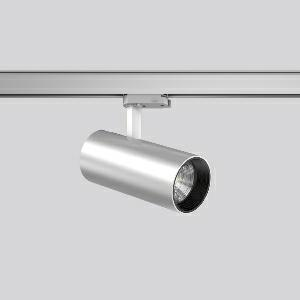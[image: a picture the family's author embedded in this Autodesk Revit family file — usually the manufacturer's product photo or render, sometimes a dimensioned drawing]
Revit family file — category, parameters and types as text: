
# Revit family: deecos_s_mini_742206_004_2_962b
name_source: partatom
category: Lighting Fixtures
units: mm (PartAtom-declared; Revit-internal decimal feet)

## family parameters
Cut with Voids When Loaded = No
Host = Face
Light Source = No
Part Type = Normal
Room Calculation Point = No
Round Connector Dimension = Use Diameter
Shared = No

## types (1)
- DEECOS S mini (1 x LED Modul 927, 3000 lm, 2700)
    Apparent Load = 29 VA
    Approval mark = CE
    CIE Flux Codes = 99 100 100 100 100
    Color Rendering = 92
    Color Temperature = 2700
    Default Elevation = 1800 mm
    Description = Series: DEECOS S mini
LED surface-mounted projector in modern design with no visible cooling ribs. Housing: die-cast aluminium, powder-coated. Rotation range: 356°. Swivel range: 90°. Black plastic ring and recessed LED to prevent glare from the side. Optical assembly with lens made of plastic (polycarbonate) for the best homogeneous light distribution - can be changed without tools. Best colour rendering index Ra>90. With multi adaptor for 3-circuit tracks 230 V. Suitable for Track on ceiling, Wall track. High quality converter without flickering and stroboscopic effect. The following accessories can be mounted without use of tools: interchangeable lenses, decorative glasses, honeycomb louvre, clear and frosted diffusers, white interchangeable plastic ring. 
Colour: silver
Diameter: 87 mm
Height: 214 mm
Lamp: LED
Socket: without socket
Colour temperature: 2700K
Colour rendering index (CRI): 92
System power: 29 W
Rated luminous flux: 3000 lm
Luminous efficiency: 103 lm/W
Control gear: Regulated power supply
Protection class: I
Type of protection: IP 20
    Height = 214 mm
    Lamp = 1 x LED Modul 927
    Lamp Light Flux = 3000 lm
    Lamp count = 1
    Length = 87 mm
    Lifetime = 50000 h
    Luminous efficacy = 103 lm/W
    Manufacturer = RZB
    ModVariant = No
    Model = 742206.004.2
    Mounting Place = Ceiling
    Mounting Type = Rail mounted
    Number of Poles = 1
    OnlyDefault = Yes
    Power Factor = 1
    Product Name = DEECOS S mini
    Product group = Track mounted projectors
    ProductGroupID = 301
    Protection Class = Protection class I
    Protection Degree = IP 20
    RLX_Detail_Level = 1
    RLX_Emergency_Light_Flux = 0 lm
    RLX_Emergency_Type = 0
    RLX_Emergency_Type_DB = No
    RlxData = <blob elided: 37185 chars, md5=dfd3fa8a>
    Socket = socket
    Standby Power = 0 W
    System Light Flux = 3000 lm
    System Power = 29 W
    Type Comments = Product without accessories
    Type Image = 741930.004.jpg
    URL = http://relux.com
    VarID = ---
    Voltage = 230 V
    Voltage Range = 220-240 V
    Weight = 0.00 kg
    Width = 0 mm  [stored 0 ft]

note: [stored X ft] marks values corroborated as IEEE doubles in the binary element streams (Revit-internal decimal feet)

## geometry (parser evidence)
native form markers: Blend x4, Sweep x13
no freeform markers — native parametric forms only
